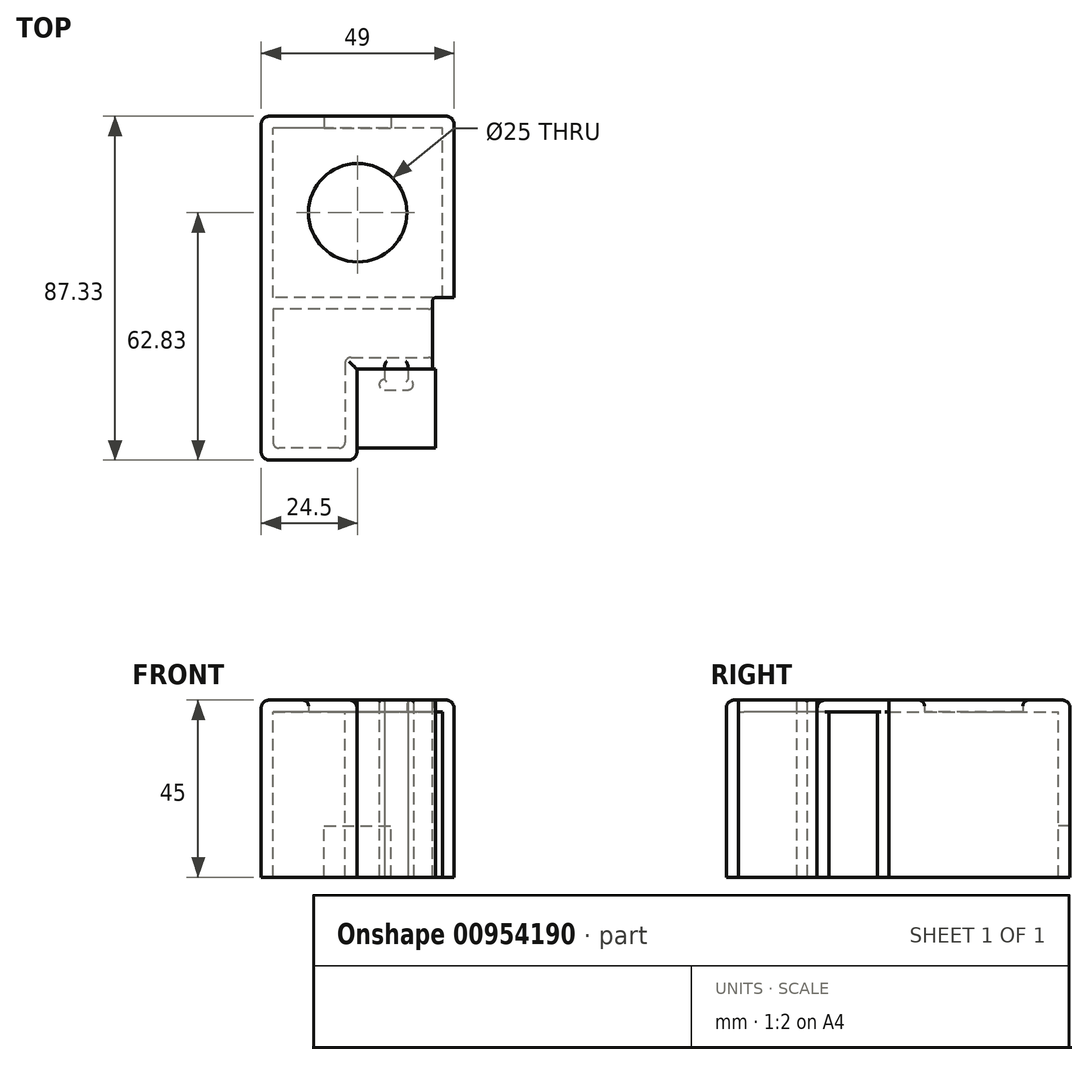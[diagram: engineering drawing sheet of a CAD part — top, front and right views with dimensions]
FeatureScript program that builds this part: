
annotation { "Feature Type Name" : "Feature", "Feature Type Description" : "" }
export const myFeature = defineFeature(function(context is Context, id is Id, definition is map)
    precondition{}
    {
        {
            var Q0;
            Q0=qCreatedBy(makeId("Top.planeOp"),FACE);
            var sketch = newSketch(context, id + "F0", { "sketchPlane" : qUnion([Q0])});
            skLineSegment(sketch, "E0.bottom", {"start": v(21.5, -21.5) * mm, "end": v(-21.5, -21.5) * mm});
            skLineSegment(sketch, "E0.top", {"start": v(21.5, 21.5) * mm, "end": v(-21.5, 21.5) * mm});
            skLineSegment(sketch, "E0.left", {"start": v(21.5, -21.5) * mm, "end": v(21.5, 21.5) * mm});
            skLineSegment(sketch, "E0.right", {"start": v(-21.5, -21.5) * mm, "end": v(-21.5, 21.5) * mm});
            skPoint(sketch, "E0.middle", {"position": v(0, 0) * mm});
            skLineSegment(sketch, "E1.0", {"start": v(24.5, -24.5) * mm, "end": v(24.5, 24.5) * mm});
            skLineSegment(sketch, "E1.1", {"start": v(24.5, -24.5) * mm, "end": v(-24.5, -24.5) * mm});
            skLineSegment(sketch, "E1.2", {"start": v(-24.5, -24.5) * mm, "end": v(-24.5, 24.5) * mm});
            skLineSegment(sketch, "E1.3", {"start": v(24.5, 24.5) * mm, "end": v(-24.5, 24.5) * mm});
            skSolve(sketch);
        }
        {
            var Q0;
            Q0=makeQuery(id+"F0.imprint","IMPRINT",FACE,{"disambiguationData":[TD([[makeQuery(id+"F0.imprint","IMPRINT",EDGE,{"derivedFrom":sQuery(id+"F0.wireOp",EDGE,"E0.bottom")}),1.0]])]});
            extrude(context, id + "F1", {"entities" : qUnion([Q0]), "oppositeDirection" : true, "depth" : 42 * mm, "offsetDistance" : 25 * mm});
        }
        {
            var Q0;
            Q0=makeQuery(id+"F0.imprint","IMPRINT",FACE,{"disambiguationData":[TD([[makeQuery(id+"F0.imprint","IMPRINT",EDGE,{"derivedFrom":sQuery(id+"F0.wireOp",EDGE,"E0.bottom")}),-1.0]])]});
            var Q1;
            Q1=makeQuery(id+"F0.imprint","IMPRINT",FACE,{"disambiguationData":[TD([[makeQuery(id+"F0.imprint","IMPRINT",EDGE,{"derivedFrom":sQuery(id+"F0.wireOp",EDGE,"E0.bottom")}),1.0]])]});
            extrude(context, id + "F2", {"entities" : qUnion([Q0, Q1]), "operationType" : NewBodyOperationType.ADD, "depth" : 3 * mm, "offsetDistance" : 25 * mm});
        }
        {
            var Q0;
            Q0=qCreatedBy(makeId("Top.planeOp"),FACE);
            var sketch = newSketch(context, id + "F3", { "sketchPlane" : qUnion([Q0])});
            skCircle(sketch, "E2", {"center": v(0, 0) * mm, "radius": 12.5 * mm});
            skSolve(sketch);
        }
        {
            var Q0;
            Q0 = qSketchRegion(id + "F3", true);
            extrude(context, id + "F4", {"entities" : qUnion([Q0]), "operationType" : NewBodyOperationType.REMOVE, "endBound" : BoundingType.THROUGH_ALL, "depth" : 25 * mm, "offsetDistance" : 25 * mm});
        }
        {
            var Q0;
            Q0=qCreatedBy(makeId("Front.planeOp"),FACE);
            var sketch = newSketch(context, id + "F5", { "sketchPlane" : qUnion([Q0])});
            skLineSegment(sketch, "E3.bottom", {"start": v(8.5, -29) * mm, "end": v(-8.5, -29) * mm});
            skLineSegment(sketch, "E4", {"start": v(8.5, -42) * mm, "end": v(-8.5, -42) * mm});
            skLineSegment(sketch, "E5", {"start": v(0, 0) * mm, "end": v(0, -42) * mm, "construction": true});
            skLineSegment(sketch, "E6", {"start": v(8.5, -29) * mm, "end": v(8.5, -42) * mm});
            skLineSegment(sketch, "E7", {"start": v(-8.5, -29) * mm, "end": v(-8.5, -42) * mm});
            skSolve(sketch);
        }
        {
            var Q0;
            Q0 = qSketchRegion(id + "F5", true);
            extrude(context, id + "F6", {"entities" : qUnion([Q0]), "operationType" : NewBodyOperationType.REMOVE, "endBound" : BoundingType.THROUGH_ALL, "oppositeDirection" : true, "depth" : 25 * mm, "offsetDistance" : 25 * mm});
        }
        {
            var Q0;
            Q0=qCreatedBy(makeId("Top.planeOp"),FACE);
            var sketch = newSketch(context, id + "F7", { "sketchPlane" : qUnion([Q0])});
            skLineSegment(sketch, "E8.bottom", {"start": v(-24.5, -24.5) * mm, "end": v(24.5, -24.5) * mm});
            skLineSegment(sketch, "E8.top", {"start": v(-0.2, -39.75) * mm, "end": v(24.5, -39.75) * mm});
            skLineSegment(sketch, "E8.left", {"start": v(-24.5, -24.5) * mm, "end": v(-24.5, -62.83) * mm});
            skLineSegment(sketch, "E8.right", {"start": v(24.5, -24.5) * mm, "end": v(24.5, -39.75) * mm});
            skLineSegment(sketch, "E9.0", {"start": v(-21.5, -24.5) * mm, "end": v(-21.5, -59.83) * mm});
            skLineSegment(sketch, "E9.2", {"start": v(21.5, -24.5) * mm, "end": v(21.5, -36.75) * mm});
            skLineSegment(sketch, "E10", {"start": v(-0.2, -39.75) * mm, "end": v(-0.2, -62.83) * mm});
            skLineSegment(sketch, "E11", {"start": v(-0.2, -62.83) * mm, "end": v(-24.5, -62.83) * mm});
            skLineSegment(sketch, "E12.0", {"start": v(-3.2, -36.75) * mm, "end": v(21.5, -36.75) * mm});
            skLineSegment(sketch, "E12.1", {"start": v(-3.2, -36.75) * mm, "end": v(-3.2, -59.83) * mm});
            skLineSegment(sketch, "E12.2", {"start": v(-3.2, -59.83) * mm, "end": v(-21.5, -59.83) * mm});
            skSolve(sketch);
        }
        {
            var Q0;
            Q0=makeQuery(id+"F7.imprint","IMPRINT",FACE,{"disambiguationData":[TD([[makeQuery(id+"F7.imprint","IMPRINT",EDGE,{"derivedFrom":sQuery(id+"F7.wireOp",EDGE,"E8.bottom")}),-1.0]])]});
            var Q1;
            Q1=makeQuery(id+"F1.opExtrude","CAP_FACE",FACE,{"disambiguationData":[OSD([sQuery(id+"F0.wireOp",EDGE,"E0.bottom"),sQuery(id+"F0.wireOp",EDGE,"E0.top"),sQuery(id+"F0.wireOp",EDGE,"E0.left"),sQuery(id+"F0.wireOp",EDGE,"E0.right"),sQuery(id+"F0.wireOp",EDGE,"E1.0"),sQuery(id+"F0.wireOp",EDGE,"E1.1"),sQuery(id+"F0.wireOp",EDGE,"E1.2"),sQuery(id+"F0.wireOp",EDGE,"E1.3")])],"isStart":false});
            var Q2;
            Q2=makeQuery(id+"F2.opExtrude","CAP_FACE",FACE,{"disambiguationData":[OSD([sQuery(id+"F0.wireOp",EDGE,"E1.0"),sQuery(id+"F0.wireOp",EDGE,"E1.1"),sQuery(id+"F0.wireOp",EDGE,"E1.2"),sQuery(id+"F0.wireOp",EDGE,"E1.3")])],"isStart":false});
            extrude(context, id + "F8", {"entities" : qUnion([Q0]), "operationType" : NewBodyOperationType.ADD, "endBound" : BoundingType.UP_TO_SURFACE, "oppositeDirection" : true, "depth" : 25 * mm, "endBoundEntityFace" : qUnion([Q1]), "offsetDistance" : 25 * mm});
        }
        {
            var Q0;
            Q0=makeQuery(id+"F7.imprint","IMPRINT",FACE,{"disambiguationData":[TD([[makeQuery(id+"F7.imprint","IMPRINT",EDGE,{"derivedFrom":sQuery(id+"F7.wireOp",EDGE,"E9.0")}),1.0]])]});
            var Q1;
            Q1=makeQuery(id+"F7.imprint","IMPRINT",FACE,{"disambiguationData":[TD([[makeQuery(id+"F7.imprint","IMPRINT",EDGE,{"derivedFrom":sQuery(id+"F7.wireOp",EDGE,"E8.bottom")}),-1.0]])]});
            var Q2;
            Q2=makeQuery(id+"F2.opExtrude","CAP_FACE",FACE,{"disambiguationData":[OSD([sQuery(id+"F0.wireOp",EDGE,"E1.0"),sQuery(id+"F0.wireOp",EDGE,"E1.1"),sQuery(id+"F0.wireOp",EDGE,"E1.2"),sQuery(id+"F0.wireOp",EDGE,"E1.3")])],"isStart":false});
            extrude(context, id + "F9", {"entities" : qUnion([Q0, Q1]), "operationType" : NewBodyOperationType.ADD, "endBound" : BoundingType.UP_TO_SURFACE, "depth" : 25 * mm, "endBoundEntityFace" : qUnion([Q2]), "offsetDistance" : 25 * mm});
        }
        {
            var Q0;
            Q0=qCreatedBy(makeId("Top.planeOp"),FACE);
            var sketch = newSketch(context, id + "F10", { "sketchPlane" : qUnion([Q0])});
            skLineSegment(sketch, "E13.bottom", {"start": v(6.8, -39.75) * mm, "end": v(12.8, -39.75) * mm});
            skLineSegment(sketch, "E13.top", {"start": v(6.8, -45) * mm, "end": v(12.8, -45) * mm});
            skLineSegment(sketch, "E13.left", {"start": v(6.8, -39.75) * mm, "end": v(6.8, -42.35) * mm});
            skLineSegment(sketch, "E13.right", {"start": v(12.8, -39.75) * mm, "end": v(12.8, -42.35) * mm});
            skArc(sketch, "E14", {"start": v(6.8, -42.35) * mm, "mid": v(5.47, -43.68) * mm, "end": v(6.8, -45) * mm});
            skArc(sketch, "E15", {"start": v(12.8, -45) * mm, "mid": v(14.12, -43.68) * mm, "end": v(12.8, -42.35) * mm});
            skSolve(sketch);
        }
        {
            var Q0;
            Q0 = qSketchRegion(id + "F10", true);
            var Q1;
            Q1=makeQuery(id+"F2.opExtrude","CAP_FACE",FACE,{"disambiguationData":[OSD([sQuery(id+"F0.wireOp",EDGE,"E1.0"),sQuery(id+"F0.wireOp",EDGE,"E1.1"),sQuery(id+"F0.wireOp",EDGE,"E1.2"),sQuery(id+"F0.wireOp",EDGE,"E1.3")])],"isStart":false});
            var Q2;
            Q2=makeQuery(id+"F1.opExtrude","CAP_FACE",FACE,{"disambiguationData":[OSD([sQuery(id+"F0.wireOp",EDGE,"E0.bottom"),sQuery(id+"F0.wireOp",EDGE,"E0.top"),sQuery(id+"F0.wireOp",EDGE,"E0.left"),sQuery(id+"F0.wireOp",EDGE,"E0.right"),sQuery(id+"F0.wireOp",EDGE,"E1.0"),sQuery(id+"F0.wireOp",EDGE,"E1.1"),sQuery(id+"F0.wireOp",EDGE,"E1.2"),sQuery(id+"F0.wireOp",EDGE,"E1.3")])],"isStart":false});
            extrude(context, id + "F11", {"entities" : qUnion([Q0]), "operationType" : NewBodyOperationType.ADD, "endBound" : BoundingType.UP_TO_SURFACE, "depth" : 25 * mm, "endBoundEntityFace" : qUnion([Q1]), "offsetDistance" : 25 * mm, "hasSecondDirection" : true, "secondDirectionBound" : SecondDirectionBoundingType.UP_TO_SURFACE, "secondDirectionOppositeDirection" : true, "secondDirectionDepth" : 25 * mm, "secondDirectionBoundEntityFace" : qUnion([Q2])});
        }
        {
            var Q0;
            Q0=qCreatedBy(makeId("Right.planeOp"),FACE);
            cPlane(context, id + "F12", {"entities" : qUnion([Q0]), "cplaneType" : CPlaneType.OFFSET, "offset" : 19 * mm, "width" : 150 * mm, "height" : 150 * mm});
        }
        {
            var Q0;
            Q0=qCreatedBy(id+"F12.planeOp",FACE);
            var sketch = newSketch(context, id + "F13", { "sketchPlane" : qUnion([Q0])});
            skLineSegment(sketch, "E16.bottom", {"start": v(-21.5, -42) * mm, "end": v(-39.75, -42) * mm});
            skLineSegment(sketch, "E16.top", {"start": v(-21.5, 3) * mm, "end": v(-39.75, 3) * mm});
            skLineSegment(sketch, "E16.left", {"start": v(-21.5, -42) * mm, "end": v(-21.5, 3) * mm});
            skLineSegment(sketch, "E16.right", {"start": v(-39.75, -42) * mm, "end": v(-39.75, 3) * mm});
            skSolve(sketch);
        }
        {
            var Q0;
            Q0 = qSketchRegion(id + "F13", true);
            var Q1;
            {var subQ0=sQuery(id+"F7.wireOp",EDGE,"E8.right");var subQ1=sQuery(id+"F0.wireOp",EDGE,"E1.0");Q1=makeQuery(id+"F9.boolean.opBoolean","MERGE",FACE,{"derivedFrom":[makeQuery(id+"F8.boolean.opBoolean","MERGE",FACE,{"derivedFrom":[makeQuery(id+"F2.boolean.opBoolean","MERGE",FACE,{"derivedFrom":[makeQuery(id+"F1.opExtrude","SWEPT_FACE",FACE,{"disambiguationData":[OSD([subQ1])]}),makeQuery(id+"F2.opExtrude","SWEPT_FACE",FACE,{"disambiguationData":[OSD([subQ1])]})]}),makeQuery(id+"F8.opExtrude","SWEPT_FACE",FACE,{"disambiguationData":[OSD([subQ0])]})]}),makeQuery(id+"F9.opExtrude","SWEPT_FACE",FACE,{"disambiguationData":[OSD([subQ0])]})]});}
            extrude(context, id + "F14", {"entities" : qUnion([Q0]), "operationType" : NewBodyOperationType.REMOVE, "endBound" : BoundingType.UP_TO_SURFACE, "depth" : 25 * mm, "endBoundEntityFace" : qUnion([Q1]), "offsetDistance" : 10 * mm, "offsetOppositeDirection" : true});
        }
        {
            var Q0;
            Q0=qCreatedBy(makeId("Top.planeOp"),FACE);
            var sketch = newSketch(context, id + "F15", { "sketchPlane" : qUnion([Q0])});
            skLineSegment(sketch, "E17", {"start": v(9.8, -45) * mm, "end": v(9.8, -49.75) * mm, "construction": true});
            skLineSegment(sketch, "E18.bottom", {"start": v(19.8, -59.75) * mm, "end": v(-0.2, -59.75) * mm});
            skLineSegment(sketch, "E18.top", {"start": v(19.8, -39.75) * mm, "end": v(-0.2, -39.75) * mm});
            skLineSegment(sketch, "E18.left", {"start": v(19.8, -59.75) * mm, "end": v(19.8, -39.75) * mm});
            skLineSegment(sketch, "E18.right", {"start": v(-0.2, -59.75) * mm, "end": v(-0.2, -39.75) * mm});
            skPoint(sketch, "E18.middle", {"position": v(9.8, -49.75) * mm});
            skSolve(sketch);
        }
        {
            var Q0;
            Q0=sQuery(id+"F15.wireOp",VERTEX,"E18.middle");
            var Q1;
            Q1=qCreatedBy(makeId("Right.planeOp"),FACE);
            cPlane(context, id + "F16", {"entities" : qUnion([Q0, Q1]), "cplaneType" : CPlaneType.PLANE_POINT, "offset" : 25 * mm, "width" : 150 * mm, "height" : 150 * mm});
        }
        {
            var Q0;
            Q0=qCreatedBy(id+"F16.planeOp",FACE);
            var sketch = newSketch(context, id + "F17", { "sketchPlane" : qUnion([Q0])});
            skLineSegment(sketch, "E19", {"start": v(-49.75, 0) * mm, "end": v(-49.75, -22.86) * mm, "construction": true});
            skSolve(sketch);
        }
        {
            var Q0;
            Q0 = qSketchRegion(id + "F15", true);
            var Q1;
            {var subQ0=sQuery(id+"F10.wireOp",EDGE,"E15");var subQ1=sQuery(id+"F10.wireOp",EDGE,"E14");var subQ2=sQuery(id+"F10.wireOp",EDGE,"E13.right");var subQ3=sQuery(id+"F10.wireOp",EDGE,"E13.left");var subQ4=sQuery(id+"F10.wireOp",EDGE,"E13.top");var subQ5=sQuery(id+"F10.wireOp",EDGE,"E13.bottom");var subQ6=sQuery(id+"F7.wireOp",EDGE,"E11");var subQ7=sQuery(id+"F7.wireOp",EDGE,"E8.left");var subQ8=sQuery(id+"F0.wireOp",EDGE,"E0.top");var subQ9=sQuery(id+"F7.wireOp",EDGE,"E9.0");var subQ10=sQuery(id+"F7.wireOp",EDGE,"E12.2");var subQ11=sQuery(id+"F0.wireOp",EDGE,"E1.3");var subQ12=sQuery(id+"F7.wireOp",EDGE,"E10");var subQ13=sQuery(id+"F0.wireOp",EDGE,"E0.right");var subQ14=sQuery(id+"F7.wireOp",EDGE,"E8.top");var subQ15=sQuery(id+"F0.wireOp",EDGE,"E0.bottom");var subQ16=sQuery(id+"F0.wireOp",EDGE,"E1.1");var subQ17=sQuery(id+"F7.wireOp",EDGE,"E12.0");var subQ18=sQuery(id+"F0.wireOp",EDGE,"E1.2");var subQ19=sQuery(id+"F7.wireOp",EDGE,"E12.1");Q1=makeQuery(id+"FOZ5Bh1tUoKdC3K_2.1.F11.boolean.opBoolean","MERGE",FACE,{"derivedFrom":[makeQuery(id+"F14.boolean.opBoolean","SPLIT",FACE,{"disambiguationData":[TD([makeQuery(id+"F1.opExtrude","SWEPT_FACE",FACE,{"disambiguationData":[OSD([subQ15])]})])],"derivedFrom":makeQuery(id+"F11.boolean.opBoolean","MERGE",FACE,{"derivedFrom":[makeQuery(id+"F8.boolean.opBoolean","MERGE",FACE,{"derivedFrom":[makeQuery(id+"F1.opExtrude","CAP_FACE",FACE,{"disambiguationData":[OSD([subQ15,subQ8,sQuery(id+"F0.wireOp",EDGE,"E0.left"),subQ13,sQuery(id+"F0.wireOp",EDGE,"E1.0"),subQ16,subQ18,subQ11])],"isStart":false}),makeQuery(id+"F8.opExtrude","CAP_FACE",FACE,{"disambiguationData":[OSD([sQuery(id+"F7.wireOp",EDGE,"E8.bottom"),subQ14,subQ7,sQuery(id+"F7.wireOp",EDGE,"E8.right"),subQ9,sQuery(id+"F7.wireOp",EDGE,"E9.2"),subQ12,subQ6,subQ17,subQ19,subQ10])],"isStart":false})]}),makeQuery(id+"F11.opExtrude","CAP_FACE",FACE,{"disambiguationData":[OSD([subQ5,subQ4,subQ3,subQ2,subQ1,subQ0])],"isStart":true})]})}),makeQuery(id+"FOZ5Bh1tUoKdC3K_2.1.F11.opExtrude","CAP_FACE",FACE,{"disambiguationData":[OSD([subQ5,subQ4,subQ3,subQ2,subQ1,subQ0])],"isStart":true})]});}
            var Q2;
            {var subQ0=sQuery(id+"F10.wireOp",EDGE,"E15");var subQ1=sQuery(id+"F10.wireOp",EDGE,"E14");var subQ2=sQuery(id+"F10.wireOp",EDGE,"E13.right");var subQ3=sQuery(id+"F10.wireOp",EDGE,"E13.left");var subQ4=sQuery(id+"F10.wireOp",EDGE,"E13.top");var subQ5=sQuery(id+"F10.wireOp",EDGE,"E13.bottom");Q2=makeQuery(id+"FOZ5Bh1tUoKdC3K_2.1.F11.boolean.opBoolean","MERGE",FACE,{"derivedFrom":[makeQuery(id+"F11.boolean.opBoolean","MERGE",FACE,{"derivedFrom":[makeQuery(id+"F9.boolean.opBoolean","MERGE",FACE,{"derivedFrom":[makeQuery(id+"F2.opExtrude","CAP_FACE",FACE,{"disambiguationData":[OSD([sQuery(id+"F0.wireOp",EDGE,"E1.0"),sQuery(id+"F0.wireOp",EDGE,"E1.1"),sQuery(id+"F0.wireOp",EDGE,"E1.2"),sQuery(id+"F0.wireOp",EDGE,"E1.3")])],"isStart":false}),makeQuery(id+"F9.opExtrude","CAP_FACE",FACE,{"disambiguationData":[OSD([sQuery(id+"F7.wireOp",EDGE,"E8.bottom"),sQuery(id+"F7.wireOp",EDGE,"E8.top"),sQuery(id+"F7.wireOp",EDGE,"E8.left"),sQuery(id+"F7.wireOp",EDGE,"E8.right"),sQuery(id+"F7.wireOp",EDGE,"E10"),sQuery(id+"F7.wireOp",EDGE,"E11")])],"isStart":false})]}),makeQuery(id+"F11.opExtrude","CAP_FACE",FACE,{"disambiguationData":[OSD([subQ5,subQ4,subQ3,subQ2,subQ1,subQ0])],"isStart":false})]}),makeQuery(id+"FOZ5Bh1tUoKdC3K_2.1.F11.opExtrude","CAP_FACE",FACE,{"disambiguationData":[OSD([subQ5,subQ4,subQ3,subQ2,subQ1,subQ0])],"isStart":false})]});}
            extrude(context, id + "F18", {"entities" : qUnion([Q0]), "endBound" : BoundingType.UP_TO_SURFACE, "oppositeDirection" : true, "depth" : 25 * mm, "endBoundEntityFace" : qUnion([Q1]), "offsetDistance" : 25 * mm, "hasSecondDirection" : true, "secondDirectionBound" : SecondDirectionBoundingType.UP_TO_SURFACE, "secondDirectionOppositeDirection" : false, "secondDirectionDepth" : 25 * mm, "secondDirectionBoundEntityFace" : qUnion([Q2])});
        }
        {
            var Q0;
            Q0=makeQuery(id+"F9.opExtrude","CAP_EDGE",EDGE,{"disambiguationData":[OSD([sQuery(id+"F7.wireOp",EDGE,"E11")])],"isStart":false});
            var Q1;
            Q1=makeQuery(id+"F9.boolean.opBoolean","MERGE",EDGE,{"derivedFrom":[makeQuery(id+"F2.opExtrude","CAP_EDGE",EDGE,{"disambiguationData":[OSD([sQuery(id+"F0.wireOp",EDGE,"E1.2")])],"isStart":false}),makeQuery(id+"F9.opExtrude","CAP_EDGE",EDGE,{"disambiguationData":[OSD([sQuery(id+"F7.wireOp",EDGE,"E8.left")])],"isStart":false})]});
            var Q2;
            Q2=makeQuery(id+"F2.opExtrude","CAP_EDGE",EDGE,{"disambiguationData":[OSD([sQuery(id+"F0.wireOp",EDGE,"E1.3")])],"isStart":false});
            var Q3;
            Q3=makeQuery(id+"F9.boolean.opBoolean","MERGE",EDGE,{"derivedFrom":[makeQuery(id+"F2.opExtrude","CAP_EDGE",EDGE,{"disambiguationData":[OSD([sQuery(id+"F0.wireOp",EDGE,"E1.0")])],"isStart":false}),makeQuery(id+"F9.opExtrude","CAP_EDGE",EDGE,{"disambiguationData":[OSD([sQuery(id+"F7.wireOp",EDGE,"E8.right")])],"isStart":false})]});
            var Q4;
            Q4=makeQuery(id+"F14.boolean.opBoolean","COPY",EDGE,{"derivedFrom":makeQuery(id+"F14.opExtrude","SWEPT_EDGE",EDGE,{"disambiguationData":[OSD([sQuery(id+"F13.wireOp",EDGE,"E16.top"),sQuery(id+"F13.wireOp",EDGE,"E16.left")])]})});
            var Q5;
            Q5=makeQuery(id+"F14.boolean.opBoolean","COPY",EDGE,{"derivedFrom":makeQuery(id+"F14.opExtrude","CAP_EDGE",EDGE,{"disambiguationData":[OSD([sQuery(id+"F13.wireOp",EDGE,"E16.top")])],"isStart":true})});
            var Q6;
            {var subQ0=sQuery(id+"F7.wireOp",EDGE,"E11");var subQ1=sQuery(id+"F7.wireOp",EDGE,"E10");Q6=makeQuery(id+"FOZ5Bh1tUoKdC3K_2.1.F11.boolean.opBoolean","SPLIT",EDGE,{"disambiguationData":[TD([makeQuery(id+"F8.opExtrude","SWEPT_FACE",FACE,{"disambiguationData":[OSD([subQ0])]})])],"derivedFrom":makeQuery(id+"F9.opExtrude","CAP_EDGE",EDGE,{"disambiguationData":[OSD([subQ1])],"isStart":false})});}
            var Q7;
            {var subQ0=sQuery(id+"F7.wireOp",EDGE,"E10");var subQ1=sQuery(id+"F7.wireOp",EDGE,"E8.top");Q7=makeQuery(id+"FOZ5Bh1tUoKdC3K_2.1.F11.boolean.opBoolean","SPLIT",EDGE,{"disambiguationData":[TD([makeQuery(id+"F8.opExtrude","SWEPT_FACE",FACE,{"disambiguationData":[OSD([subQ1])]})])],"derivedFrom":makeQuery(id+"F9.opExtrude","CAP_EDGE",EDGE,{"disambiguationData":[OSD([subQ0])],"isStart":false})});}
            var Q8;
            {var subQ0=sQuery(id+"F7.wireOp",EDGE,"E10");var subQ1=sQuery(id+"F7.wireOp",EDGE,"E8.top");Q8=makeQuery(id+"F11.boolean.opBoolean","SPLIT",EDGE,{"disambiguationData":[TD([makeQuery(id+"F8.opExtrude","SWEPT_FACE",FACE,{"disambiguationData":[OSD([subQ0])]})])],"derivedFrom":makeQuery(id+"F9.opExtrude","CAP_EDGE",EDGE,{"disambiguationData":[OSD([subQ1])],"isStart":false})});}
            var Q9;
            {var subQ0=sQuery(id+"F7.wireOp",EDGE,"E8.top");var subQ2=sQuery(id+"F0.wireOp",EDGE,"E1.0");Q9=makeQuery(id+"F11.boolean.opBoolean","SPLIT",EDGE,{"disambiguationData":[TD([makeQuery(id+"F1.opExtrude","SWEPT_FACE",FACE,{"disambiguationData":[OSD([subQ2])]})])],"derivedFrom":makeQuery(id+"F9.opExtrude","CAP_EDGE",EDGE,{"disambiguationData":[OSD([subQ0])],"isStart":false})});}
            var Q10;
            {var subQ0=sQuery(id+"F7.wireOp",EDGE,"E11");var subQ1=sQuery(id+"F7.wireOp",EDGE,"E10");Q10=makeQuery(id+"F9.boolean.opBoolean","MERGE",EDGE,{"derivedFrom":[makeQuery(id+"F8.opExtrude","SWEPT_EDGE",EDGE,{"disambiguationData":[OSD([subQ1,subQ0])]}),makeQuery(id+"F9.opExtrude","SWEPT_EDGE",EDGE,{"disambiguationData":[OSD([subQ1,subQ0])]})]});}
            var Q11;
            {var subQ0=sQuery(id+"F7.wireOp",EDGE,"E11");var subQ1=sQuery(id+"F7.wireOp",EDGE,"E8.left");Q11=makeQuery(id+"F9.boolean.opBoolean","MERGE",EDGE,{"derivedFrom":[makeQuery(id+"F8.opExtrude","SWEPT_EDGE",EDGE,{"disambiguationData":[OSD([subQ1,subQ0])]}),makeQuery(id+"F9.opExtrude","SWEPT_EDGE",EDGE,{"disambiguationData":[OSD([subQ1,subQ0])]})]});}
            var Q12;
            {var subQ0=sQuery(id+"F0.wireOp",EDGE,"E1.3");var subQ1=sQuery(id+"F0.wireOp",EDGE,"E1.2");Q12=makeQuery(id+"F2.boolean.opBoolean","MERGE",EDGE,{"derivedFrom":[makeQuery(id+"F1.opExtrude","SWEPT_EDGE",EDGE,{"disambiguationData":[OSD([subQ1,subQ0])]}),makeQuery(id+"F2.opExtrude","SWEPT_EDGE",EDGE,{"disambiguationData":[OSD([subQ1,subQ0])]})]});}
            var Q13;
            {var subQ0=sQuery(id+"F0.wireOp",EDGE,"E1.3");var subQ1=sQuery(id+"F0.wireOp",EDGE,"E1.0");Q13=makeQuery(id+"F2.boolean.opBoolean","MERGE",EDGE,{"derivedFrom":[makeQuery(id+"F1.opExtrude","SWEPT_EDGE",EDGE,{"disambiguationData":[OSD([subQ1,subQ0])]}),makeQuery(id+"F2.opExtrude","SWEPT_EDGE",EDGE,{"disambiguationData":[OSD([subQ1,subQ0])]})]});}
            var Q14;
            Q14=makeQuery(id+"F14.boolean.opBoolean","COPY",EDGE,{"derivedFrom":makeQuery(id+"F14.opExtrude","CAP_EDGE",EDGE,{"disambiguationData":[OSD([sQuery(id+"F13.wireOp",EDGE,"E16.left")])],"isStart":false})});
            fillet(context, id + "F19", {"entities" : qUnion([Q0, Q1, Q2, Q3, Q4, Q5, Q6, Q7, Q8, Q9, Q10, Q11, Q12, Q13, Q14]), "radius" : 2 * mm, "tangentPropagation" : true, "allowEdgeOverflow" : false});
        }
        {
            var Q0;
            Q0=makeQuery(id+"FOZ5Bh1tUoKdC3K_2.1.F11.opExtrude","CAP_EDGE",EDGE,{"disambiguationData":[OSD([sQuery(id+"F10.wireOp",EDGE,"E13.left")])],"isStart":false});
            var Q1;
            Q1=makeQuery(id+"FOZ5Bh1tUoKdC3K_2.1.F11.opExtrude","CAP_EDGE",EDGE,{"disambiguationData":[OSD([sQuery(id+"F10.wireOp",EDGE,"E13.top")])],"isStart":false});
            var Q2;
            Q2=makeQuery(id+"FOZ5Bh1tUoKdC3K_2.1.F11.opExtrude","CAP_EDGE",EDGE,{"disambiguationData":[OSD([sQuery(id+"F10.wireOp",EDGE,"E14")])],"isStart":false});
            var Q3;
            Q3=makeQuery(id+"FOZ5Bh1tUoKdC3K_2.1.F11.opExtrude","CAP_EDGE",EDGE,{"disambiguationData":[OSD([sQuery(id+"F10.wireOp",EDGE,"E13.right")])],"isStart":false});
            var Q4;
            Q4=makeQuery(id+"FOZ5Bh1tUoKdC3K_2.1.F11.opExtrude","CAP_EDGE",EDGE,{"disambiguationData":[OSD([sQuery(id+"F10.wireOp",EDGE,"E15")])],"isStart":false});
            var Q5;
            Q5=makeQuery(id+"F11.opExtrude","CAP_EDGE",EDGE,{"disambiguationData":[OSD([sQuery(id+"F10.wireOp",EDGE,"E13.left")])],"isStart":false});
            var Q6;
            Q6=makeQuery(id+"F11.opExtrude","CAP_EDGE",EDGE,{"disambiguationData":[OSD([sQuery(id+"F10.wireOp",EDGE,"E14")])],"isStart":false});
            var Q7;
            Q7=makeQuery(id+"F11.opExtrude","CAP_EDGE",EDGE,{"disambiguationData":[OSD([sQuery(id+"F10.wireOp",EDGE,"E13.right")])],"isStart":false});
            var Q8;
            Q8=makeQuery(id+"F11.opExtrude","CAP_EDGE",EDGE,{"disambiguationData":[OSD([sQuery(id+"F10.wireOp",EDGE,"E15")])],"isStart":false});
            var Q9;
            Q9=makeQuery(id+"F11.opExtrude","CAP_EDGE",EDGE,{"disambiguationData":[OSD([sQuery(id+"F10.wireOp",EDGE,"E13.top")])],"isStart":false});
            fillet(context, id + "F20", {"entities" : qUnion([Q0, Q1, Q2, Q3, Q4, Q5, Q6, Q7, Q8, Q9]), "radius" : .5 * mm, "tangentPropagation" : true, "allowEdgeOverflow" : false});
        }
        {
            var Q0;
            Q0=makeQuery(id+"F4.boolean.opBoolean","INTERSECT",EDGE,{"derivedFrom":[makeQuery(id+"F2.opExtrude","CAP_FACE",FACE,{"disambiguationData":[OSD([sQuery(id+"F0.wireOp",EDGE,"E1.0"),sQuery(id+"F0.wireOp",EDGE,"E1.1"),sQuery(id+"F0.wireOp",EDGE,"E1.2"),sQuery(id+"F0.wireOp",EDGE,"E1.3")])],"isStart":false}),makeQuery(id+"F4.opExtrude","SWEPT_FACE",FACE,{"disambiguationData":[OSD([sQuery(id+"F3.wireOp",EDGE,"E2")])]})]});
            var Q1;
            Q1=makeQuery(id+"F4.boolean.opBoolean","COPY",EDGE,{"derivedFrom":makeQuery(id+"F4.opExtrude","CAP_EDGE",EDGE,{"disambiguationData":[OSD([sQuery(id+"F3.wireOp",EDGE,"E2")])],"isStart":true})});
            var Q2;
            Q2=makeQuery(id+"F9.opExtrude","CAP_EDGE",EDGE,{"disambiguationData":[OSD([sQuery(id+"F7.wireOp",EDGE,"E8.bottom")])],"isStart":true});
            var Q3;
            Q3=makeQuery(id+"F8.opExtrude","CAP_EDGE",EDGE,{"disambiguationData":[OSD([sQuery(id+"F7.wireOp",EDGE,"E12.0")])],"isStart":true});
            var Q4;
            Q4=makeQuery(id+"F8.opExtrude","CAP_EDGE",EDGE,{"disambiguationData":[OSD([sQuery(id+"F7.wireOp",EDGE,"E9.0")])],"isStart":true});
            var Q5;
            Q5=makeQuery(id+"F8.opExtrude","CAP_EDGE",EDGE,{"disambiguationData":[OSD([sQuery(id+"F7.wireOp",EDGE,"E12.1")])],"isStart":true});
            var Q6;
            Q6=makeQuery(id+"F8.opExtrude","CAP_EDGE",EDGE,{"disambiguationData":[OSD([sQuery(id+"F7.wireOp",EDGE,"E12.2")])],"isStart":true});
            var Q7;
            Q7=makeQuery(id+"F8.opExtrude","SWEPT_EDGE",EDGE,{"disambiguationData":[OSD([sQuery(id+"F7.wireOp",EDGE,"E8.bottom"),sQuery(id+"F7.wireOp",EDGE,"E9.0")])]});
            var Q8;
            Q8=makeQuery(id+"F8.opExtrude","SWEPT_EDGE",EDGE,{"disambiguationData":[OSD([sQuery(id+"F7.wireOp",EDGE,"E9.0"),sQuery(id+"F7.wireOp",EDGE,"E12.2")])]});
            var Q9;
            Q9=makeQuery(id+"F8.opExtrude","SWEPT_EDGE",EDGE,{"disambiguationData":[OSD([sQuery(id+"F7.wireOp",EDGE,"E12.1"),sQuery(id+"F7.wireOp",EDGE,"E12.2")])]});
            var Q10;
            Q10=makeQuery(id+"F8.opExtrude","SWEPT_EDGE",EDGE,{"disambiguationData":[OSD([sQuery(id+"F7.wireOp",EDGE,"E12.0"),sQuery(id+"F7.wireOp",EDGE,"E12.1")])]});
            fillet(context, id + "F21", {"entities" : qUnion([Q0, Q1, Q2, Q3, Q4, Q5, Q6, Q7, Q8, Q9, Q10]), "radius" : 1.5 * mm, "tangentPropagation" : true, "allowEdgeOverflow" : false});
        }
        {
            var Q0;
            Q0=makeQuery(id+"F14.boolean.opBoolean","COPY",EDGE,{"derivedFrom":makeQuery(id+"F14.opExtrude","CAP_EDGE",EDGE,{"disambiguationData":[OSD([sQuery(id+"F13.wireOp",EDGE,"E16.right")])],"isStart":true})});
            var Q1;
            Q1=makeQuery(id+"F14.boolean.opBoolean","INTERSECT",EDGE,{"derivedFrom":[makeQuery(id+"F8.opExtrude","SWEPT_FACE",FACE,{"disambiguationData":[OSD([sQuery(id+"F7.wireOp",EDGE,"E12.0")])]}),makeQuery(id+"F14.opExtrude","CAP_FACE",FACE,{"disambiguationData":[OSD([sQuery(id+"F13.wireOp",EDGE,"E16.bottom"),sQuery(id+"F13.wireOp",EDGE,"E16.top"),sQuery(id+"F13.wireOp",EDGE,"E16.left"),sQuery(id+"F13.wireOp",EDGE,"E16.right")])],"isStart":true})]});
            var Q2;
            {var subQ0=sQuery(id+"F0.wireOp",EDGE,"E1.1");Q2=makeQuery(id+"F14.boolean.opBoolean","INTERSECT",EDGE,{"derivedFrom":[makeQuery(id+"F2.boolean.opBoolean","MERGE",FACE,{"derivedFrom":[makeQuery(id+"F1.opExtrude","SWEPT_FACE",FACE,{"disambiguationData":[OSD([subQ0])]}),makeQuery(id+"F2.opExtrude","SWEPT_FACE",FACE,{"disambiguationData":[OSD([subQ0])]})]}),makeQuery(id+"F14.opExtrude","CAP_FACE",FACE,{"disambiguationData":[OSD([sQuery(id+"F13.wireOp",EDGE,"E16.bottom"),sQuery(id+"F13.wireOp",EDGE,"E16.top"),sQuery(id+"F13.wireOp",EDGE,"E16.left"),sQuery(id+"F13.wireOp",EDGE,"E16.right")])],"isStart":true})]});}
            var Q3;
            {var subQ0=sQuery(id+"F13.wireOp",EDGE,"E16.left");Q3=makeQuery(id+"F14.boolean.opBoolean","COPY",EDGE,{"disambiguationData":[topologyDisambiguationEdgeConnected([makeQuery(id+"F1.opExtrude","SWEPT_FACE",FACE,{"disambiguationData":[OSD([sQuery(id+"F0.wireOp",EDGE,"E0.bottom")])]})])],"derivedFrom":makeQuery(id+"F14.opExtrude","CAP_EDGE",EDGE,{"disambiguationData":[OSD([subQ0])],"isStart":true})});}
            fillet(context, id + "F22", {"entities" : qUnion([Q0, Q1, Q2, Q3]), "radius" : 1 * mm, "tangentPropagation" : true, "allowEdgeOverflow" : false});
        }
    });
